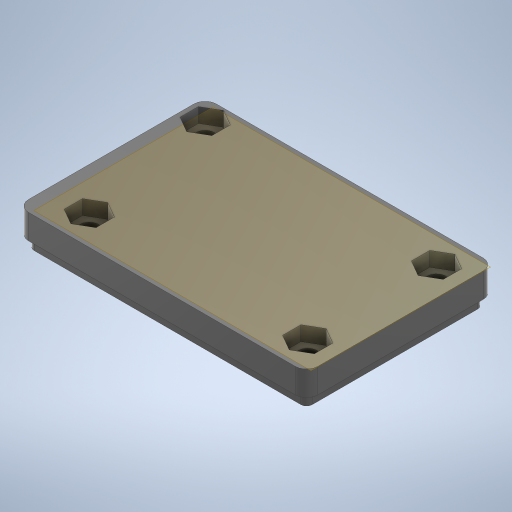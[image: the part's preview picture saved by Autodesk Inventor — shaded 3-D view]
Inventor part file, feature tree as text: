
AUTODESK INVENTOR PART (.ipt)
format: ipt  version: 2024 (Build 280153000, 153)  size: 423,424 bytes
history: native  units: mm
features: extrude x8, sketch x8, projected_geometry x6, other x6, reference x5, plane x3, fillet x2
ambient origin geometry x8: Origin, YZ Plane, XZ Plane, XY Plane, X Axis, Y Axis, Z Axis, Center Point
bodies: Body1 (feature_tree)
feature tree (38):
  plane  "Arbeitsebene1"
  extrude  "Extrusion2"  Depth=2.6mm
  sketch  "Skizze4"  dims[d7=2.0mm d8=0.0mm d9=2.0mm]
  plane  "Arbeitsebene2"
  extrude  "Extrusion3"  Depth=2.0mm
  extrude  "Extrusion4"  Depth=1.0mm
  sketch  "Skizze6"  dims[d13=2.0mm d14=0.0mm d15=0.2mm]
  plane  "Arbeitsebene3"
  extrude  "Extrusion5"  Depth=0.2mm
  extrude  "Extrusion6"  Depth=0.2mm
  extrude  "Extrusion7"  Depth=6.6mm
  fillet  "Rundung1"  Radius=2.0mm
  fillet  "Rundung2"  Radius=6.2mm
  extrude  "Extrusion8"  Depth=6.6mm
  extrude  "Extrusion9"  Depth=2.0mm
  sketch  "Skizze3"  dims[d5=2.2mm d6=2.6mm]
  reference  "Referenz3"
  reference  "Referenz4"
  projected_geometry  "Projizierte Kontur2"
  sketch  "Skizze5"  dims[d10=2.0mm d11=0.0mm d12=1.0mm]
  projected_geometry  "Projizierte Kontur3"
  reference  "Referenz5"
  reference  "Referenz6"
  reference  "Referenz7"
  sketch  "Skizze7"  dims[d16=0.2mm d17=0.2mm]
  projected_geometry  "Projizierte Kontur4"
  projected_geometry  "Projizierte Kontur5"
  projected_geometry  "Projizierte Kontur6"
  sketch  "Skizze8"  dims[d18=6.2mm d19=6.6mm d20=2.0mm d21=6.2mm]
  projected_geometry  "Projizierte Kontur7"
  sketch  "Skizze9"  dims[d22=6.6mm d23=3.3mm]
  sketch  "Skizze10"  dims[d24=3.1mm d25=2.0mm d26=2.0mm d27=2.211mm d28=0.0mm d29=2.8mm d30=0.0mm d31=5.7mm d32=5.7mm d33=5.7mm d34=2.6mm d35=0.0mm d36=2.0mm d37=1.0mm d38=3.3mm d39=3.3mm d40=10.0mm d41=0.0mm d42=5.7mm d43=2.6mm d44=0.0mm]
  parser-record x1  (decoder bookkeeping rows leaked as tree rows — omitted from the tree; the rows remain in map.json)
  other  "main.iam"
  other  "Umgebungssensor_PCB:1"
  other  "GY-BME280:1"
  other  "Finish1"
  other  "Finish2"
note: 1 file-system path scrubbed to <path> (originals preserved in map.json)
